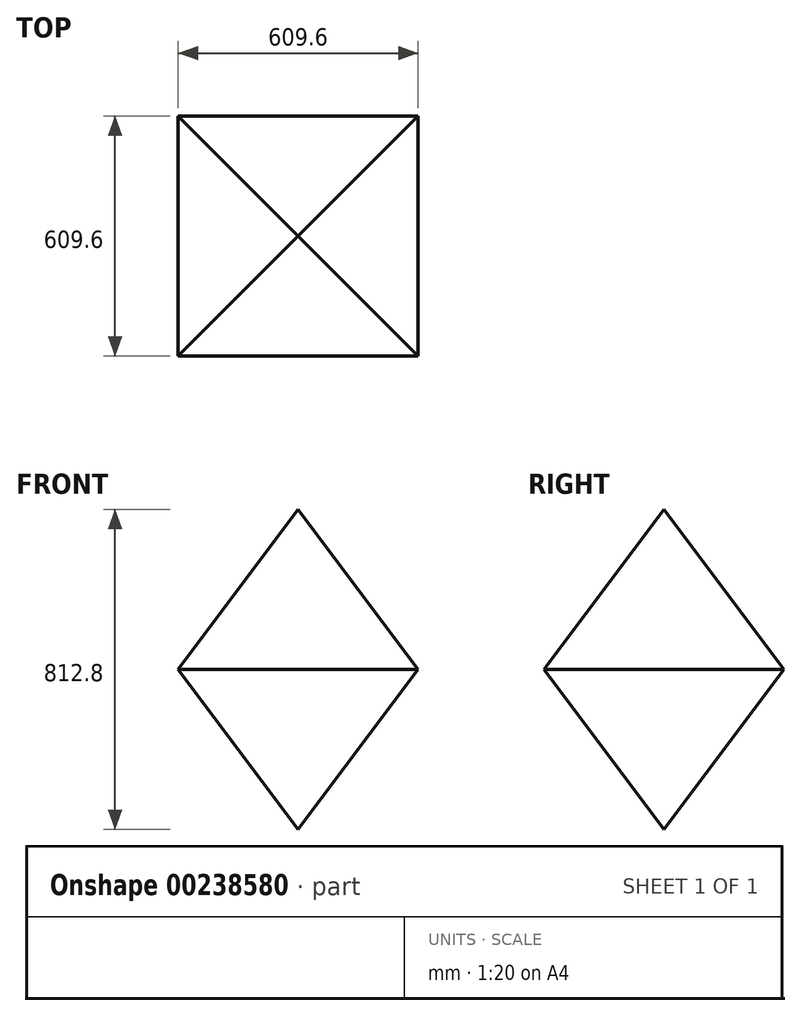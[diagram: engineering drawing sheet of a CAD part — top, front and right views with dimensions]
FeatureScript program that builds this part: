
annotation { "Feature Type Name" : "Feature", "Feature Type Description" : "" }
export const myFeature = defineFeature(function(context is Context, id is Id, definition is map)
    precondition{}
    {
        {
            assignVariable(context, id + "F0", {"name" : "l", "anyValue" : 609.6 * mm});
        }
        {
            var Q0;
            Q0=qCreatedBy(makeId("Top.planeOp"),FACE);
            var sketch = newSketch(context, id + "F1", { "sketchPlane" : qUnion([Q0])});
            skLineSegment(sketch, "E0.bottom", {"start": v(304.8, 304.8) * mm, "end": v(-304.8, 304.8) * mm});
            skLineSegment(sketch, "E0.top", {"start": v(304.8, -304.8) * mm, "end": v(-304.8, -304.8) * mm});
            skLineSegment(sketch, "E0.left", {"start": v(304.8, 304.8) * mm, "end": v(304.8, -304.8) * mm});
            skLineSegment(sketch, "E0.right", {"start": v(-304.8, 304.8) * mm, "end": v(-304.8, -304.8) * mm});
            skPoint(sketch, "E0.middle", {"position": v(0, 0) * mm});
            skSolve(sketch);
        }
        {
            assignVariable(context, id + "F2", {"name" : "h", "anyValue" : getVariable(context, 'l') / 1.5});
        }
        {
            var Q0;
            Q0=qCreatedBy(makeId("Top.planeOp"),FACE);
            cPlane(context, id + "F3", {"entities" : qUnion([Q0]), "cplaneType" : CPlaneType.OFFSET, "offset" : getVariable(context, 'h'), "width" : 152.4 * mm, "height" : 152.4 * mm});
        }
        {
            var Q0;
            Q0=qCreatedBy(makeId("Top.planeOp"),FACE);
            cPlane(context, id + "F4", {"entities" : qUnion([Q0]), "cplaneType" : CPlaneType.OFFSET, "offset" : getVariable(context, 'h'), "oppositeDirection" : true, "width" : 152.4 * mm, "height" : 152.4 * mm});
        }
        {
            var Q0;
            Q0=qCreatedBy(id+"F3.planeOp",FACE);
            var sketch = newSketch(context, id + "F5", { "sketchPlane" : qUnion([Q0])});
            skPoint(sketch, "E1", {"position": v(0, 0) * mm});
            skSolve(sketch);
        }
        {
            var Q0;
            Q0=qCreatedBy(id+"F4.planeOp",FACE);
            var sketch = newSketch(context, id + "F6", { "sketchPlane" : qUnion([Q0])});
            skPoint(sketch, "E2", {"position": v(0, 0) * mm});
            skSolve(sketch);
        }
        {
            var Q0;
            Q0=makeQuery(id+"F1.imprint","IMPRINT",FACE,{"disambiguationData":[TD([[makeQuery(id+"F1.imprint","IMPRINT",EDGE,{"derivedFrom":sQuery(id+"F1.wireOp",EDGE,"E0.bottom")}),1.0]])]});
            var Q1;
            Q1=sQuery(id+"F5.wireOp",VERTEX,"E1");
            loft(context, id + "F7", {"sheetProfilesArray" : [{ "sheetProfileEntities" : qUnion([Q0]) }, { "sheetProfileEntities" : qUnion([Q1]) }]});
        }
        {
            var Q1;
            Q1=makeQuery(id+"F7.opLoft","CAP_FACE",FACE,{"disambiguationData":[OSD([makeQuery(id+"F1.imprint","IMPRINT",FACE,{"disambiguationData":[TD([[makeQuery(id+"F1.imprint","IMPRINT",EDGE,{"derivedFrom":sQuery(id+"F1.wireOp",EDGE,"E0.bottom")}),1.0]])]})])],"isStart":true});
            var Q2;
            Q2=sQuery(id+"F6.wireOp",VERTEX,"E2");
            loft(context, id + "F8", {"operationType" : NewBodyOperationType.ADD, "sheetProfilesArray" : [{ "sheetProfileEntities" : qUnion([Q1]) }, { "sheetProfileEntities" : qUnion([Q2]) }]});
        }
    });
